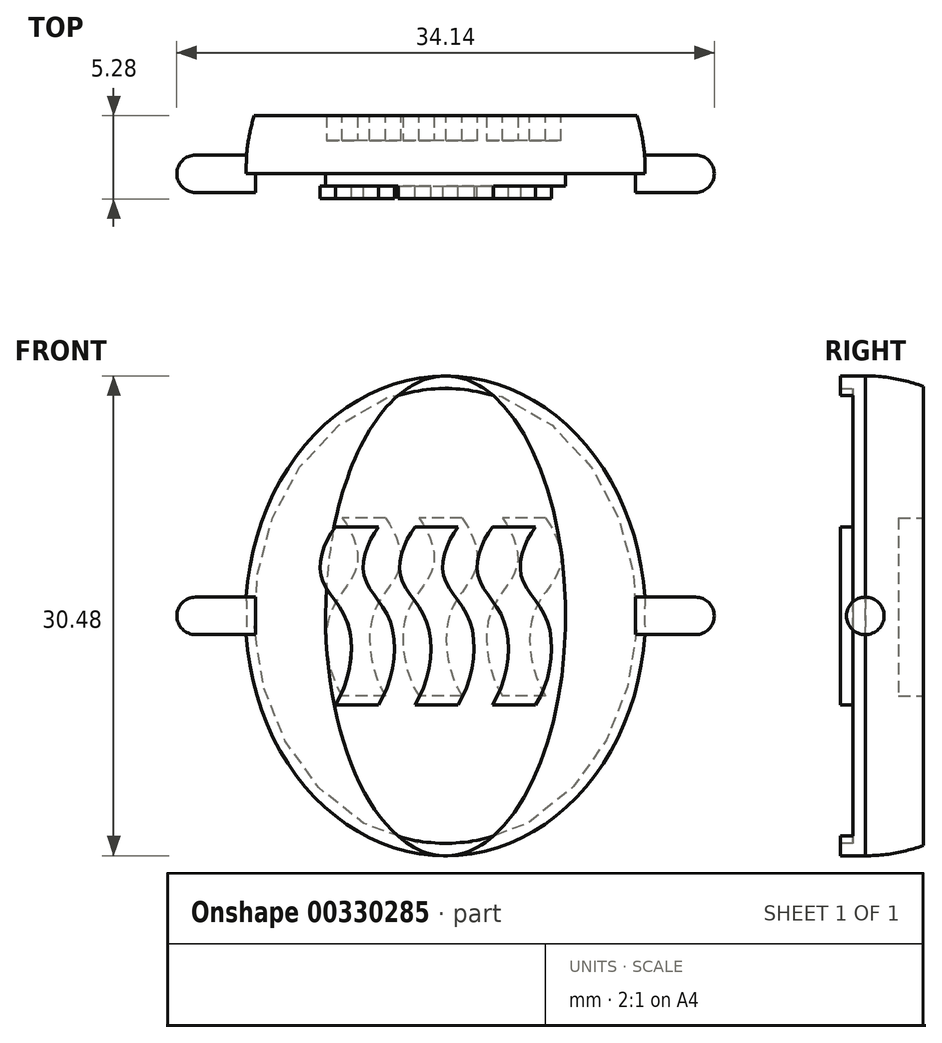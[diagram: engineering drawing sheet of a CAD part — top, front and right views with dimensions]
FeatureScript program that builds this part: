
annotation { "Feature Type Name" : "Feature", "Feature Type Description" : "" }
export const myFeature = defineFeature(function(context is Context, id is Id, definition is map)
    precondition{}
    {
        {
            var Q0;
            Q0=qCreatedBy(makeId("Front.planeOp"),FACE);
            var sketch = newSketch(context, id + "F0", { "sketchPlane" : qUnion([Q0])});
            skEllipticalArc(sketch, "E0", {});
            skLineSegment(sketch, "E1", {"start": v(0, 15.24) * mm, "end": v(0, -15.24) * mm});
            const initialGuessF0  = {"E0": [0, 0, 0, 1, 0.01524, 0.0127, 3.141592653589793, 0]};
            skSetInitialGuess(sketch, initialGuessF0);
            skSolve(sketch);
        }
        {
            var Q0;
            Q0 = qSketchRegion(id + "F0", true);
            var Q1;
            Q1=sQuery(id+"F0.wireOp",EDGE,"E1");
            revolve(context, id + "F1", {"entities" : qUnion([Q0]), "axis" : qUnion([Q1]), "revolveType" : RevolveType.ONE_DIRECTION, "oppositeDirection" : true, "angle" : 180 * degree});
        }
        {
            var Q0;
            Q0=qCreatedBy(makeId("Right.planeOp"),FACE);
            var sketch = newSketch(context, id + "F2", { "sketchPlane" : qUnion([Q0])});
            skLineSegment(sketch, "E2.bottom", {"start": v(3.69, 15.9) * mm, "end": v(30.72, 15.9) * mm});
            skLineSegment(sketch, "E2.top", {"start": v(3.69, -22.6) * mm, "end": v(30.72, -22.6) * mm});
            skLineSegment(sketch, "E2.left", {"start": v(3.69, 15.9) * mm, "end": v(3.69, -22.6) * mm});
            skLineSegment(sketch, "E2.right", {"start": v(30.72, 15.9) * mm, "end": v(30.72, -22.6) * mm});
            skSolve(sketch);
        }
        {
            var Q0;
            Q0 = qSketchRegion(id + "F2", true);
            extrude(context, id + "F3", {"entities" : qUnion([Q0]), "operationType" : NewBodyOperationType.REMOVE, "oppositeDirection" : true, "depth" : 50.8 * mm, "symmetric" : true});
        }
        {
            var Q0;
            Q0=makeQuery(id+"F1.opRevolve","CAP_FACE",FACE,{"disambiguationData":[OSD([sQuery(id+"F0.wireOp",EDGE,"E0"),sQuery(id+"F0.wireOp",EDGE,"E1")])],"isStart":false});
            var sketch = newSketch(context, id + "F4", { "sketchPlane" : qUnion([Q0])});
            skEllipticalArc(sketch, "E3.0", {});
            skEllipticalArc(sketch, "E3.1", {});
            const initialGuessF4  = {"E3.0": [0, 0, 0, 1, 0.01524, 0.00762, 0, 3.141592653589793], "E3.1": [0, 0, 0, 1, 0.01524, 0.00762, 3.141592653589793, 0]};
            skSetInitialGuess(sketch, initialGuessF4);
            skSolve(sketch);
        }
        {
            var Q0;
            Q0 = qSketchRegion(id + "F4", true);
            extrude(context, id + "F5", {"entities" : qUnion([Q0]), "operationType" : NewBodyOperationType.ADD, "depth" : 1.59 * mm});
        }
        {
            var Q0;
            Q0=makeQuery(id+"F5.opExtrude","CAP_FACE",FACE,{"disambiguationData":[OSD([sQuery(id+"F4.wireOp",EDGE,"E3.0"),sQuery(id+"F4.wireOp",EDGE,"E3.1")])],"isStart":false});
            var sketch = newSketch(context, id + "F6", { "sketchPlane" : qUnion([Q0])});
            skEllipse(sketch, "E4", {"center": v(0, 0) * mm, "majorRadius": 14.45 * mm, "minorRadius": 12.07 * mm, "majorAxis": v(0, 1)});
            skSolve(sketch);
        }
        {
            var Q0;
            Q0 = qSketchRegion(id + "F6", true);
            extrude(context, id + "F7", {"entities" : qUnion([Q0]), "operationType" : NewBodyOperationType.REMOVE, "oppositeDirection" : true, "depth" : 0.8 * mm});
        }
        {
            var Q0;
            Q0=makeQuery(id+"F7.boolean.opBoolean","COPY",FACE,{"derivedFrom":makeQuery(id+"F7.opExtrude","CAP_FACE",FACE,{"disambiguationData":[OSD([sQuery(id+"F6.wireOp",EDGE,"E4")])],"isStart":false})});
            var sketch = newSketch(context, id + "F8", { "sketchPlane" : qUnion([Q0])});
            skSolve(sketch);
        }
        {
            var Q0;
            Q0=makeQuery(id+"F8.imprint","IMPRINT",FACE,{"disambiguationData":[TD([[makeQuery(id+"F8.imprint","IMPRINT",EDGE,{"derivedFrom":makeQuery(id+"F7.boolean.opBoolean","COPY",EDGE,{"derivedFrom":makeQuery(id+"F7.opExtrude","CAP_EDGE",EDGE,{"disambiguationData":[OSD([sQuery(id+"F6.wireOp",EDGE,"E4")])],"isStart":false})})}),1.0]])]});
            var sketch = newSketch(context, id + "F9", { "sketchPlane" : qUnion([Q0])});
            skLineSegment(sketch, "E5", {"start": v(-7, 5.66) * mm, "end": v(-4.26, 5.66) * mm});
            skLineSegment(sketch, "E6.MirrorCS", {"start": v(-7, -5.66) * mm, "end": v(-4.26, -5.66) * mm});
            skFitSpline(sketch, "E7", {"points": [v(-7, 5.66) * mm, v(-7.92, 2.6) * mm, v(-6.23, -0.43) * mm, v(-7, -5.66) * mm], "startDerivative": vector(-6.3, -8.44) * mm, "endDerivative": vector(-7.2, -11.43) * mm});
            skFitSpline(sketch, "E8", {"points": [v(-4.26, 5.66) * mm, v(-5.18, 2.6) * mm, v(-3.5, -0.43) * mm, v(-4.26, -5.66) * mm], "startDerivative": vector(-6.3, -8.44) * mm, "endDerivative": vector(-7.2, -11.43) * mm});
            skLineSegment(sketch, "E9", {"start": v(-1.94, 5.66) * mm, "end": v(0.8, 5.66) * mm});
            skLineSegment(sketch, "E10.MirrorCS", {"start": v(-1.94, -5.66) * mm, "end": v(0.8, -5.66) * mm});
            skFitSpline(sketch, "E11", {"points": [v(-1.94, 5.66) * mm, v(-2.87, 2.6) * mm, v(-1.18, -0.43) * mm, v(-1.94, -5.66) * mm], "startDerivative": vector(-6.3, -8.44) * mm, "endDerivative": vector(-7.2, -11.43) * mm});
            skFitSpline(sketch, "E12", {"points": [v(0.8, 5.66) * mm, v(-0.13, 2.6) * mm, v(1.56, -0.43) * mm, v(0.8, -5.66) * mm], "startDerivative": vector(-6.3, -8.44) * mm, "endDerivative": vector(-7.2, -11.43) * mm});
            skLineSegment(sketch, "E13", {"start": v(2.98, 5.66) * mm, "end": v(5.72, 5.66) * mm});
            skLineSegment(sketch, "E14.MirrorCS", {"start": v(2.98, -5.66) * mm, "end": v(5.72, -5.66) * mm});
            skFitSpline(sketch, "E15", {"points": [v(2.98, 5.66) * mm, v(2.05, 2.6) * mm, v(3.75, -0.43) * mm, v(2.98, -5.66) * mm], "startDerivative": vector(-6.3, -8.44) * mm, "endDerivative": vector(-7.2, -11.43) * mm});
            skFitSpline(sketch, "E16", {"points": [v(5.72, 5.66) * mm, v(4.8, 2.6) * mm, v(6.49, -0.43) * mm, v(5.72, -5.66) * mm], "startDerivative": vector(-6.3, -8.44) * mm, "endDerivative": vector(-7.2, -11.43) * mm});
            skSolve(sketch);
        }
        {
            var Q0;
            Q0 = qSketchRegion(id + "F9", true);
            extrude(context, id + "F10", {"entities" : qUnion([Q0]), "operationType" : NewBodyOperationType.ADD, "depth" : 0.8 * mm});
        }
        {
            var Q0;
            Q0=makeQuery(id+"F3.boolean.opBoolean","COPY",FACE,{"derivedFrom":makeQuery(id+"F3.opExtrude","SWEPT_FACE",FACE,{"disambiguationData":[OSD([sQuery(id+"F2.wireOp",EDGE,"E2.left")])]})});
            var sketch = newSketch(context, id + "F11", { "sketchPlane" : qUnion([Q0])});
            skLineSegment(sketch, "E17", {"start": v(-6.35, 6.22) * mm, "end": v(-3.6, 6.22) * mm});
            skLineSegment(sketch, "E18.MirrorCS", {"start": v(-6.35, -5.09) * mm, "end": v(-3.6, -5.09) * mm});
            skFitSpline(sketch, "E19", {"points": [v(-6.35, 6.22) * mm, v(-7.28, 3.16) * mm, v(-5.58, 0.13) * mm, v(-6.35, -5.09) * mm], "startDerivative": vector(-6.3, -8.44) * mm, "endDerivative": vector(-7.2, -11.43) * mm});
            skFitSpline(sketch, "E20", {"points": [v(-3.6, 6.22) * mm, v(-4.54, 3.16) * mm, v(-2.84, 0.13) * mm, v(-3.6, -5.09) * mm], "startDerivative": vector(-6.3, -8.44) * mm, "endDerivative": vector(-7.2, -11.43) * mm});
            skLineSegment(sketch, "E21", {"start": v(-1.04, 6.22) * mm, "end": v(1.7, 6.22) * mm});
            skLineSegment(sketch, "E22.MirrorCS", {"start": v(-1.04, -5.09) * mm, "end": v(1.7, -5.09) * mm});
            skFitSpline(sketch, "E23", {"points": [v(-1.04, 6.22) * mm, v(-1.97, 3.16) * mm, v(-0.28, 0.13) * mm, v(-1.04, -5.09) * mm], "startDerivative": vector(-6.3, -8.44) * mm, "endDerivative": vector(-7.2, -11.43) * mm});
            skFitSpline(sketch, "E24", {"points": [v(1.7, 6.22) * mm, v(0.77, 3.16) * mm, v(2.46, 0.13) * mm, v(1.7, -5.09) * mm], "startDerivative": vector(-6.3, -8.44) * mm, "endDerivative": vector(-7.2, -11.43) * mm});
            skLineSegment(sketch, "E25", {"start": v(3.82, 6.22) * mm, "end": v(6.56, 6.22) * mm});
            skLineSegment(sketch, "E26.MirrorCS", {"start": v(3.82, -5.09) * mm, "end": v(6.56, -5.09) * mm});
            skFitSpline(sketch, "E27", {"points": [v(3.82, 6.22) * mm, v(2.9, 3.16) * mm, v(4.59, 0.13) * mm, v(3.82, -5.09) * mm], "startDerivative": vector(-6.3, -8.44) * mm, "endDerivative": vector(-7.2, -11.43) * mm});
            skFitSpline(sketch, "E28", {"points": [v(6.56, 6.22) * mm, v(5.63, 3.16) * mm, v(7.33, 0.13) * mm, v(6.56, -5.09) * mm], "startDerivative": vector(-6.3, -8.44) * mm, "endDerivative": vector(-7.2, -11.43) * mm});
            skSolve(sketch);
        }
        {
            var Q0;
            Q0 = qSketchRegion(id + "F11", true);
            extrude(context, id + "F12", {"entities" : qUnion([Q0]), "operationType" : NewBodyOperationType.REMOVE, "oppositeDirection" : true, "depth" : 1.59 * mm});
        }
        {
            var Q0;
            Q0=qCreatedBy(makeId("Right.planeOp"),FACE);
            cPlane(context, id + "F13", {"entities" : qUnion([Q0]), "cplaneType" : CPlaneType.OFFSET, "offset" : 12.7 * mm, "width" : 152.4 * mm, "height" : 152.4 * mm});
        }
        {
            var Q0;
            Q0=qCreatedBy(id+"F13.planeOp",FACE);
            var sketch = newSketch(context, id + "F14", { "sketchPlane" : qUnion([Q0])});
            skCircle(sketch, "E29", {"center": v(0, 0) * mm, "radius": 1.2 * mm});
            skSolve(sketch);
        }
        {
            var Q0;
            Q0 = qSketchRegion(id + "F14", true);
            extrude(context, id + "F15", {"entities" : qUnion([Q0]), "operationType" : NewBodyOperationType.ADD, "depth" : 3.17 * mm, "hasSecondDirection" : true, "secondDirectionOppositeDirection" : true, "secondDirectionDepth" : 0.64 * mm});
        }
        {
            var Q0;
            Q0=makeQuery(id+"F15.opExtrude","CAP_FACE",FACE,{"disambiguationData":[OSD([sQuery(id+"F14.wireOp",EDGE,"E29")])],"isStart":false});
            var sketch = newSketch(context, id + "F16", { "sketchPlane" : qUnion([Q0])});
            skArc(sketch, "E30.0", {"start": v(1.2, 0) * mm, "mid": v(0, 1.2) * mm, "end": v(-1.2, 0) * mm});
            skLineSegment(sketch, "E31", {"start": v(1.2, 0) * mm, "end": v(-1.2, 0) * mm});
            skSolve(sketch);
        }
        {
            var Q0;
            Q0 = qSketchRegion(id + "F16", true);
            var Q1;
            Q1=sQuery(id+"F16.wireOp",EDGE,"E31");
            revolve(context, id + "F17", {"operationType" : NewBodyOperationType.ADD, "entities" : qUnion([Q0]), "axis" : qUnion([Q1]), "revolveType" : RevolveType.ONE_DIRECTION, "oppositeDirection" : true, "angle" : 180 * degree});
        }
        {
            var Q0;
            Q0=qCreatedBy(makeId("Right.planeOp"),FACE);
            cPlane(context, id + "F18", {"entities" : qUnion([Q0]), "cplaneType" : CPlaneType.OFFSET, "offset" : 12.7 * mm, "oppositeDirection" : true, "width" : 152.4 * mm, "height" : 152.4 * mm});
        }
        {
            var Q0;
            Q0=qCreatedBy(id+"F18.planeOp",FACE);
            var sketch = newSketch(context, id + "F19", { "sketchPlane" : qUnion([Q0])});
            skCircle(sketch, "E32.0", {"center": v(0, 0) * mm, "radius": 1.2 * mm});
            skSolve(sketch);
        }
        {
            var Q0;
            Q0 = qSketchRegion(id + "F19", true);
            extrude(context, id + "F20", {"entities" : qUnion([Q0]), "operationType" : NewBodyOperationType.ADD, "oppositeDirection" : true, "depth" : 3.17 * mm, "hasSecondDirection" : true, "secondDirectionOppositeDirection" : false, "secondDirectionDepth" : 0.64 * mm});
        }
        {
            var Q0;
            Q0=makeQuery(id+"F20.opExtrude","CAP_FACE",FACE,{"disambiguationData":[OSD([sQuery(id+"F19.wireOp",EDGE,"E32.0")])],"isStart":false});
            var sketch = newSketch(context, id + "F21", { "sketchPlane" : qUnion([Q0])});
            skArc(sketch, "E33.0", {"start": v(1.2, 0) * mm, "mid": v(0, 1.2) * mm, "end": v(-1.2, 0) * mm});
            skLineSegment(sketch, "E34", {"start": v(1.2, 0) * mm, "end": v(-1.2, 0) * mm});
            skSolve(sketch);
        }
        {
            var Q0;
            Q0 = qSketchRegion(id + "F21", true);
            var Q1;
            Q1=sQuery(id+"F21.wireOp",EDGE,"E34");
            revolve(context, id + "F22", {"operationType" : NewBodyOperationType.ADD, "entities" : qUnion([Q0]), "axis" : qUnion([Q1]), "revolveType" : RevolveType.FULL});
        }
    });
